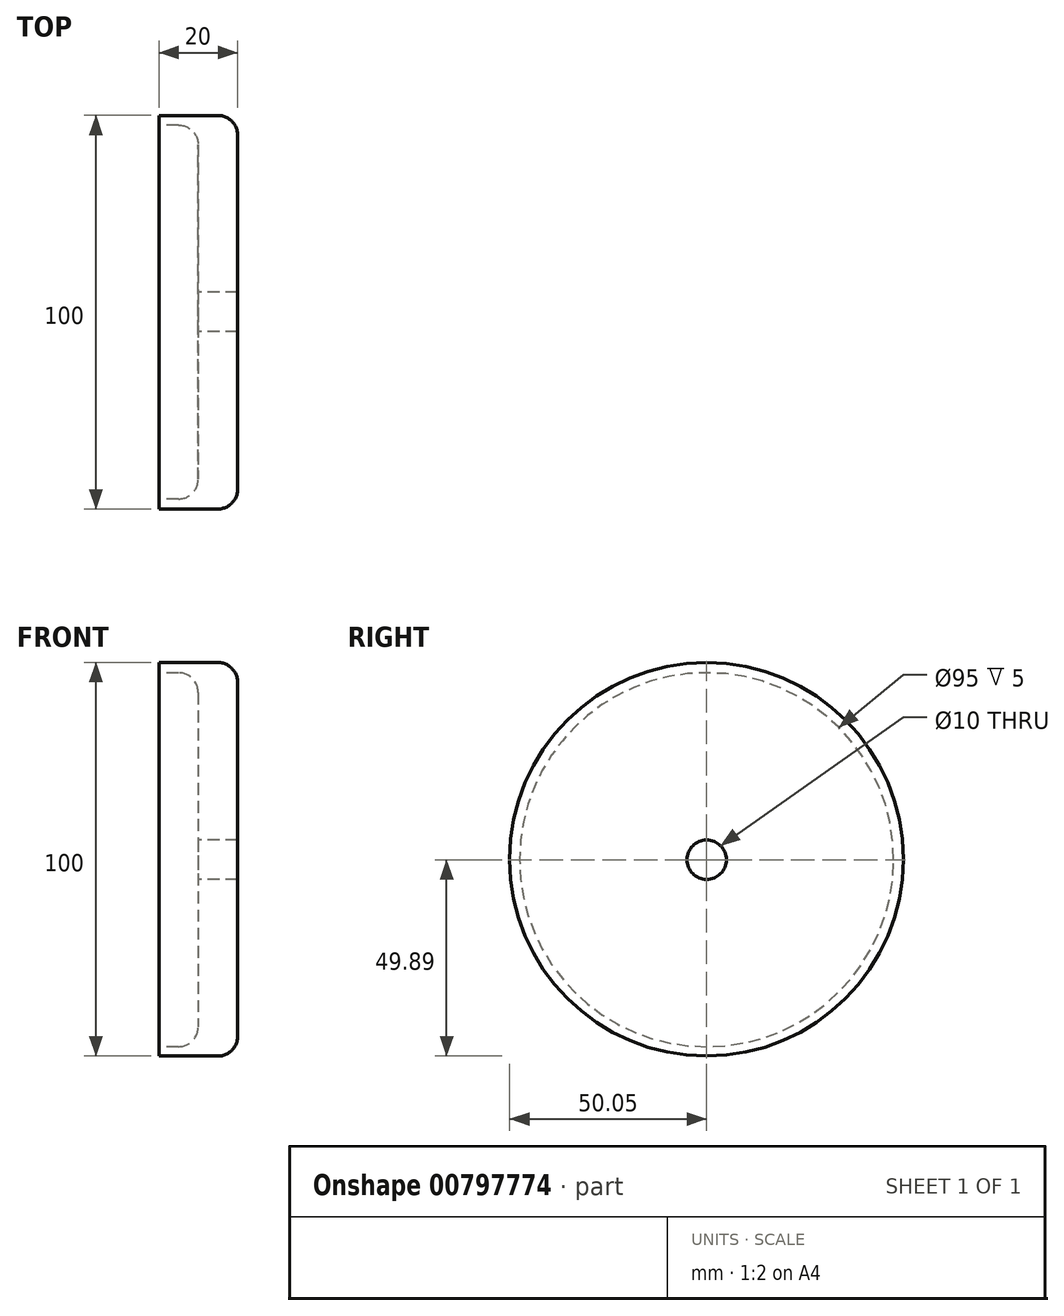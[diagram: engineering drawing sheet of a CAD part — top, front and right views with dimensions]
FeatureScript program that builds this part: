
annotation { "Feature Type Name" : "Feature", "Feature Type Description" : "" }
export const myFeature = defineFeature(function(context is Context, id is Id, definition is map)
    precondition{}
    {
        {
            var Q0;
            Q0=qCreatedBy(makeId("Right.planeOp"),FACE);
            var sketch = newSketch(context, id + "F0", { "sketchPlane" : qUnion([Q0])});
            skCircle(sketch, "E0", {"center": v(-0.05, 0.1) * mm, "radius": 50 * mm});
            skSolve(sketch);
        }
        {
            var Q0;
            Q0 = qSketchRegion(id + "F0", true);
            extrude(context, id + "F1", {"entities" : qUnion([Q0]), "depth" : 20 * mm, "offsetDistance" : 25 * mm});
        }
        {
            var Q0;
            Q0=makeQuery(id+"F1.opExtrude","CAP_FACE",FACE,{"disambiguationData":[OSD([sQuery(id+"F0.wireOp",EDGE,"E0")])],"isStart":true});
            var sketch = newSketch(context, id + "F2", { "sketchPlane" : qUnion([Q0])});
            skCircle(sketch, "E1", {"center": v(0, 0) * mm, "radius": 47.5 * mm});
            skSolve(sketch);
        }
        {
            var Q0;
            Q0=makeQuery(id+"F2.imprint","IMPRINT",FACE,{"disambiguationData":[TD([[makeQuery(id+"F2.imprint","IMPRINT",EDGE,{"derivedFrom":sQuery(id+"F2.wireOp",EDGE,"E1")}),1.0]])]});
            extrude(context, id + "F3", {"entities" : qUnion([Q0]), "operationType" : NewBodyOperationType.REMOVE, "oppositeDirection" : true, "depth" : 10 * mm, "offsetDistance" : 25 * mm});
        }
        {
            var Q0;
            Q0=makeQuery(id+"F3.boolean.opBoolean","COPY",EDGE,{"derivedFrom":makeQuery(id+"F3.opExtrude","CAP_EDGE",EDGE,{"disambiguationData":[OSD([sQuery(id+"F2.wireOp",EDGE,"E1")])],"isStart":false})});
            fillet(context, id + "F4", {"entities" : qUnion([Q0]), "radius" : 5 * mm, "tangentPropagation" : true, "allowEdgeOverflow" : false});
        }
        {
            var Q0;
            Q0=makeQuery(id+"F3.boolean.opBoolean","COPY",FACE,{"derivedFrom":makeQuery(id+"F3.opExtrude","CAP_FACE",FACE,{"disambiguationData":[OSD([sQuery(id+"F2.wireOp",EDGE,"E1")])],"isStart":false})});
            var Q1;
            Q1=makeQuery(id+"F1.opExtrude","CAP_EDGE",EDGE,{"disambiguationData":[OSD([sQuery(id+"F0.wireOp",EDGE,"E0")])],"isStart":false});
            fillet(context, id + "F5", {"entities" : qUnion([Q0, Q1]), "radius" : 5 * mm, "tangentPropagation" : true, "allowEdgeOverflow" : false});
        }
        {
            var Q0;
            Q0=makeQuery(id+"F3.boolean.opBoolean","COPY",FACE,{"derivedFrom":makeQuery(id+"F3.opExtrude","CAP_FACE",FACE,{"disambiguationData":[OSD([sQuery(id+"F2.wireOp",EDGE,"E1")])],"isStart":false})});
            var sketch = newSketch(context, id + "F6", { "sketchPlane" : qUnion([Q0])});
            skCircle(sketch, "E2", {"center": v(0, 0) * mm, "radius": 5 * mm});
            skSolve(sketch);
        }
        {
            var Q0;
            Q0=makeQuery(id+"F6.imprint","IMPRINT",FACE,{"disambiguationData":[TD([[makeQuery(id+"F6.imprint","IMPRINT",EDGE,{"derivedFrom":sQuery(id+"F6.wireOp",EDGE,"E2")}),1.0]])]});
            extrude(context, id + "F7", {"entities" : qUnion([Q0]), "operationType" : NewBodyOperationType.REMOVE, "oppositeDirection" : true, "depth" : 25 * mm, "offsetDistance" : 25 * mm});
        }
    });
